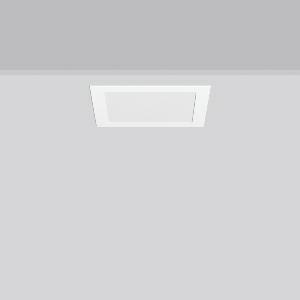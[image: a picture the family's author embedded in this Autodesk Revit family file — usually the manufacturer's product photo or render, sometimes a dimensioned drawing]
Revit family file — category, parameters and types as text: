
# Revit family: toledo_flat_square_e_901670_002_76_b49c
name_source: partatom
category: Lighting Fixtures
units: mm (PartAtom-declared; Revit-internal decimal feet)

## family parameters
Cut with Voids When Loaded = No
Host = Face
Light Source = No
Part Type = Normal
Room Calculation Point = No
Round Connector Dimension = Use Diameter
Shared = No

## types (1)
- TuneableWhite 846 (1 x LED Modul 846, 1600 lm, 4600)
    Apparent Load = 19 VA
    CIE Flux Codes = 48 79 96 100 100
    Color Rendering = 80
    Color Temperature = 4600
    Default Elevation = 1800 mm
    Description = Series: TOLEDO FLAT square
Ultra thin recessed downlight. Housing: die-cast aluminium. Light guide and diffuser made of non-yellowing PMMA, opal matt. Tunable white dynamically adjustable from 2700 K to 6500 K. Ceiling installation with spring system. Mounting depth depends on ceiling strength. Surface mounted housing as accessory for all sizes. Retrofittable decorative cylinders made of chintz fabric as accessory, optional with satin finish plastic diffuser. Through-wiring box (5 pole) available as accessory. 
Colour: white
Length: 225 mm
Width: 225 mm
Height: 3 mm
Cut-out length: 208 mm
Cut-out width: 208 mm
Recess height: 29-56 mm
Luminaire: recess height: 31-51 mm
Lamp: LED
Socket: without socket
Colour temperature: 2700K - 6500K
Colour rendering index (CRI): 80
System power: 19 W
Rated luminous flux: 1600 lm
Luminous efficiency: 84 lm/W
System power 2: 20 W
Rated luminous flux 2: 1500 lm
Luminous efficiency 2: 75 lm/W
System power 3: 18 W
Rated luminous flux 3: 1550 lm
Luminous efficiency 3: 86 lm/W
Control gear: Converter, dimmable, DALI
Protection class: II
Type of protection: IP 54
    Height = 0 mm  [stored 0 ft]
    Lamp = 1 x LED Modul 846
    Lamp Light Flux = 1600 lm
    Lamp count = 1
    Length = 225 mm
    Lifetime = 50000 h
    Luminous efficacy = 84 lm/W
    Manufacturer = RZB
    ModVariant = No
    Model = 901670.002.76
    Mounting Place = Ceiling
    Mounting Type = Recessed
    Number of Poles = 1
    OnlyDefault = Yes
    Power Factor = 1
    Product Name = TOLEDO FLAT square E
    Product group = Recessed downlights
    ProductGroupID = 402
    Protection Class = Protection class II
    Protection Degree = IP 20
    RLX_Detail_Level = 1
    RLX_Emergency_Light_Flux = 0 lm
    RLX_Emergency_Type = 0
    RLX_Emergency_Type_DB = No
    RlxData = <blob elided: 58741 chars, md5=9bd0aa4f>
    Socket = socket
    Standby Power = 0 W
    System Light Flux = 1600 lm
    System Power = 19 W
    Type Comments = TuneableWhite 846
    Type Image = 901487.002.jpg
    URL = http://relux.com
    VarID = tuneablewhite_846
    Voltage = 230 V
    Voltage Range = 220-240 V
    Weight = 0.00 kg
    Width = 225 mm

note: [stored X ft] marks values corroborated as IEEE doubles in the binary element streams (Revit-internal decimal feet)

## geometry (parser evidence)
native form markers: Blend x4, Sweep x10
no freeform markers — native parametric forms only
